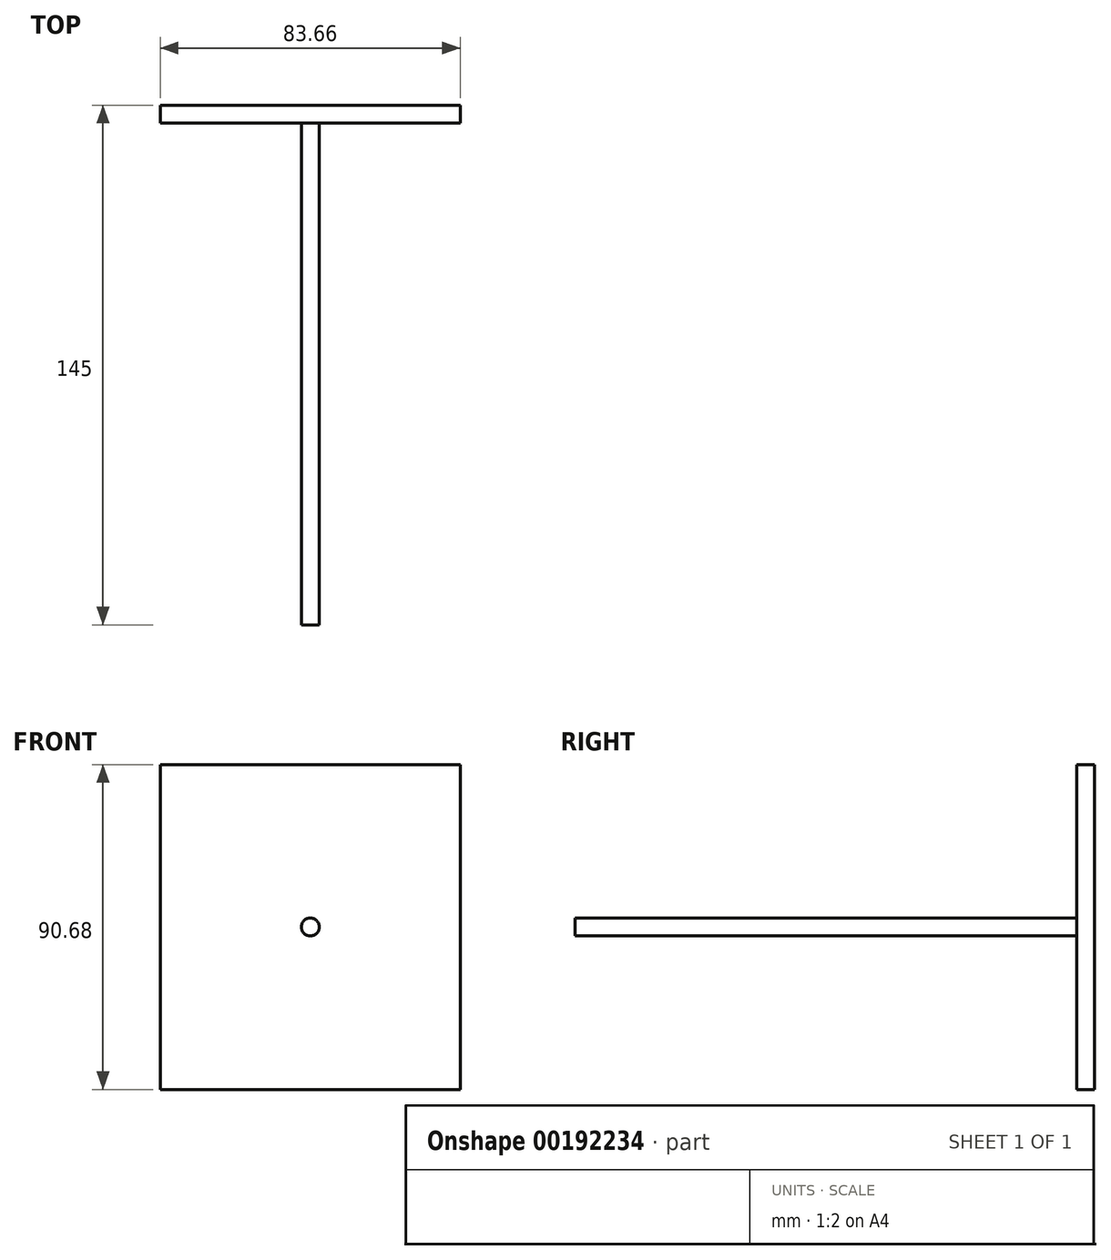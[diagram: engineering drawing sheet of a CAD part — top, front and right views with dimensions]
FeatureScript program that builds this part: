
annotation { "Feature Type Name" : "Feature", "Feature Type Description" : "" }
export const myFeature = defineFeature(function(context is Context, id is Id, definition is map)
    precondition{}
    {
        {
            var Q0;
            Q0=qCreatedBy(makeId("Front.planeOp"),FACE);
            var sketch = newSketch(context, id + "F0", { "sketchPlane" : qUnion([Q0])});
            skLineSegment(sketch, "E0.bottom", {"start": v(41.83, 45.34) * mm, "end": v(-41.83, 45.34) * mm});
            skLineSegment(sketch, "E0.top", {"start": v(41.83, -45.34) * mm, "end": v(-41.83, -45.34) * mm});
            skLineSegment(sketch, "E0.left", {"start": v(41.83, 45.34) * mm, "end": v(41.83, -45.34) * mm});
            skLineSegment(sketch, "E0.right", {"start": v(-41.83, 45.34) * mm, "end": v(-41.83, -45.34) * mm});
            skPoint(sketch, "E0.middle", {"position": v(0, 0) * mm});
            skSolve(sketch);
        }
        {
            var Q0;
            Q0 = qSketchRegion(id + "F0", true);
            extrude(context, id + "F1", {"entities" : qUnion([Q0]), "depth" : 5 * mm});
        }
        {
            var Q0;
            Q0=makeQuery(id+"F1.opExtrude","CAP_FACE",FACE,{"disambiguationData":[OSD([sQuery(id+"F0.wireOp",EDGE,"E0.bottom"),sQuery(id+"F0.wireOp",EDGE,"E0.top"),sQuery(id+"F0.wireOp",EDGE,"E0.left"),sQuery(id+"F0.wireOp",EDGE,"E0.right")])],"isStart":false});
            var sketch = newSketch(context, id + "F2", { "sketchPlane" : qUnion([Q0])});
            skCircle(sketch, "E1", {"center": v(0, 0) * mm, "radius": 2.5 * mm});
            skSolve(sketch);
        }
        {
            var Q0;
            Q0 = qSketchRegion(id + "F2", true);
            extrude(context, id + "F3", {"entities" : qUnion([Q0]), "operationType" : NewBodyOperationType.ADD, "depth" : 140 * mm});
        }
    });
